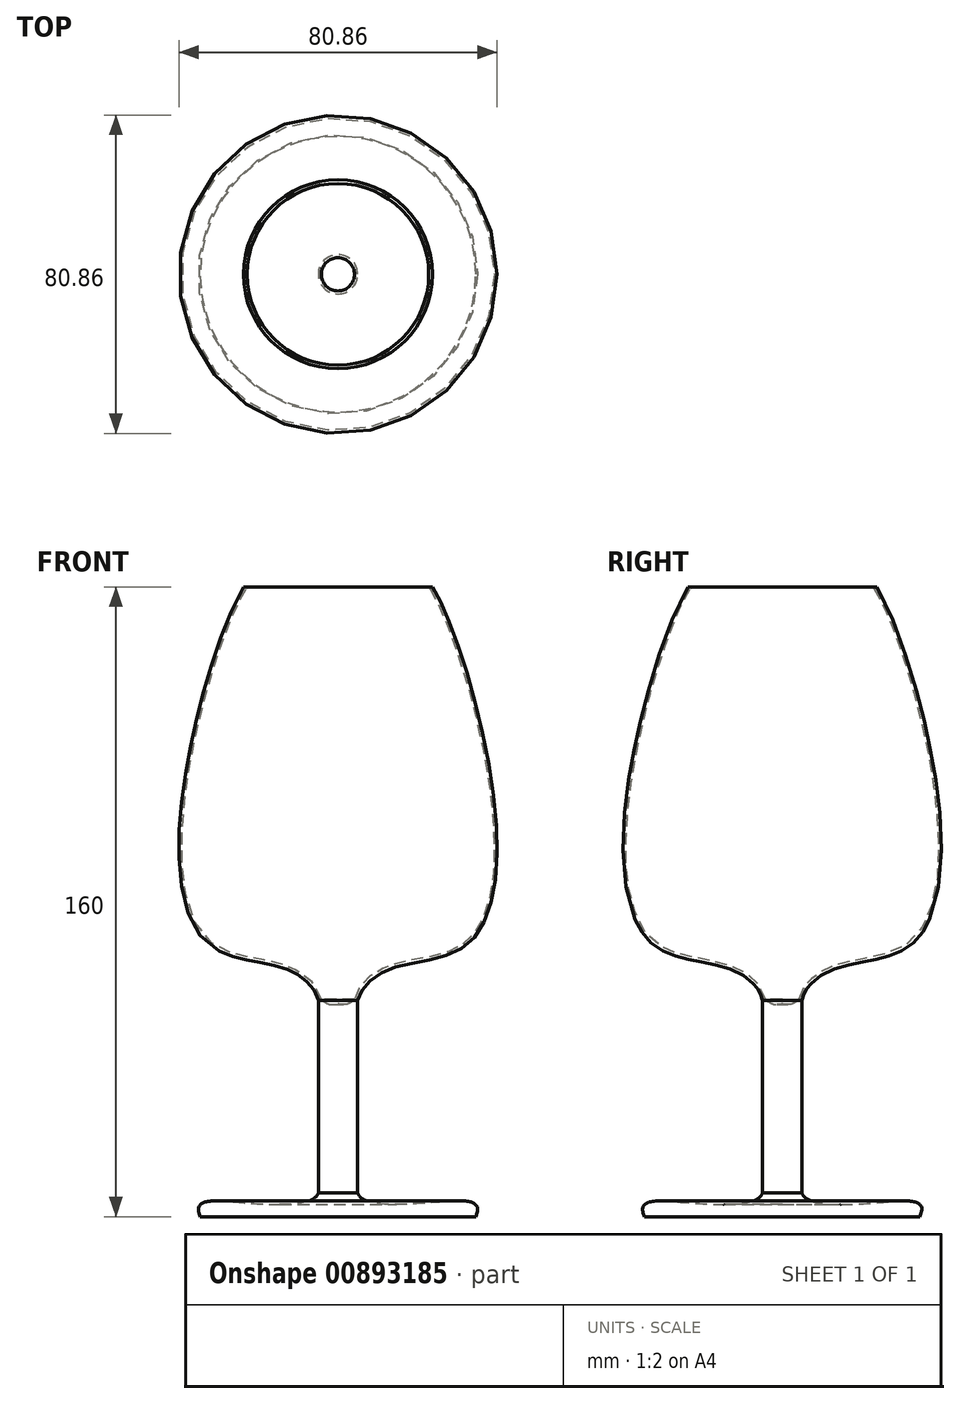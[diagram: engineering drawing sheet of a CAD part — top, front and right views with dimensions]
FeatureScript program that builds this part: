
annotation { "Feature Type Name" : "Feature", "Feature Type Description" : "" }
export const myFeature = defineFeature(function(context is Context, id is Id, definition is map)
    precondition{}
    {
        {
            var Q0;
            Q0=qCreatedBy(makeId("Front.planeOp"),FACE);
            var sketch = newSketch(context, id + "F0", { "sketchPlane" : qUnion([Q0])});
            skLineSegment(sketch, "E0", {"start": v(-35, 0) * mm, "end": v(0, 0) * mm});
            skLineSegment(sketch, "E1", {"start": v(-5, 55) * mm, "end": v(-5, 6) * mm});
            skFitSpline(sketch, "E2", {"points": [v(-35, 0) * mm, v(-35, 3) * mm, v(-31.51, 4) * mm, v(-5, 6) * mm], "startDerivative": vector(-12.01, 31.79) * mm, "endDerivative": vector(9.66, 26.35) * mm});
            skFitSpline(sketch, "E3", {"points": [v(-24, 160) * mm, v(-39.4, 108.3) * mm, v(-33, 69.28) * mm, v(-13.07, 62.86) * mm, v(-5, 55) * mm], "startDerivative": vector(-43.56, -70.12) * mm, "endDerivative": vector(11.53, -58.94) * mm});
            skLineSegment(sketch, "E4", {"start": v(0, 141.93) * mm, "end": v(0, -21.73) * mm, "construction": true});
            skFitSpline(sketch, "E5.0", {"points": [v(-23.32, 159.58) * mm, v(-23.76, 158.87) * mm, v(-24.7, 157.2) * mm, v(-26.72, 152.88) * mm, v(-29.43, 145.96) * mm, v(-32.68, 135.89) * mm, v(-35.14, 126.6) * mm, v(-36.8, 118.98) * mm, v(-37.87, 113.25) * mm, v(-38.72, 107.6) * mm, v(-39.3, 102.1) * mm, v(-39.63, 96.82) * mm, v(-39.67, 90.12) * mm, v(-39.1, 84.06) * mm, v(-37.88, 78.85) * mm, v(-36.61, 75.43) * mm, v(-35, 72.54) * mm, v(-33.37, 70.62) * mm, v(-31.89, 69.4) * mm, v(-30.27, 68.34) * mm, v(-28.02, 67.32) * mm, v(-25.06, 66.44) * mm, v(-21.95, 65.78) * mm, v(-18.8, 65.2) * mm, v(-16.22, 64.66) * mm, v(-14.25, 64.13) * mm, v(-12.82, 63.65) * mm, v(-11.47, 63.08) * mm, v(-9.8, 62.2) * mm, v(-7.93, 60.92) * mm, v(-6.14, 59.16) * mm, v(-4.84, 57.22) * mm, v(-4.35, 55.85) * mm, v(-4.21, 55.15) * mm]});
            skLineSegment(sketch, "E6", {"start": v(-24, 160) * mm, "end": v(-23.06, 160) * mm});
            skLineSegment(sketch, "E7", {"start": v(-23.32, 159.58) * mm, "end": v(-23.06, 160) * mm});
            skFitSpline(sketch, "E8", {"points": [v(-4.21, 55.15) * mm, v(-2.02, 53.93) * mm, v(0, 54.04) * mm], "startDerivative": vector(4.93, -4.12) * mm, "endDerivative": vector(4.3, 0.83) * mm});
            skLineSegment(sketch, "E9", {"start": v(0, 0) * mm, "end": v(0, 54.04) * mm});
            skSolve(sketch);
        }
        {
            var Q0;
            Q0 = qSketchRegion(id + "F0", true);
            var Q1;
            Q1 = qConstructionFilter(qBodyType(qCreatedBy(id + "F0" ,EDGE), BodyType.WIRE), ConstructionObject.NO);
            var Q2;
            Q2=sQuery(id+"F0.wireOp",EDGE,"E4");
            revolve(context, id + "F1", {"surfaceOperationType" : NewSurfaceOperationType.ADD, "entities" : qUnion([Q0]), "surfaceEntities" : qUnion([Q1]), "axis" : qUnion([Q2]), "revolveType" : RevolveType.FULL});
        }
    });
